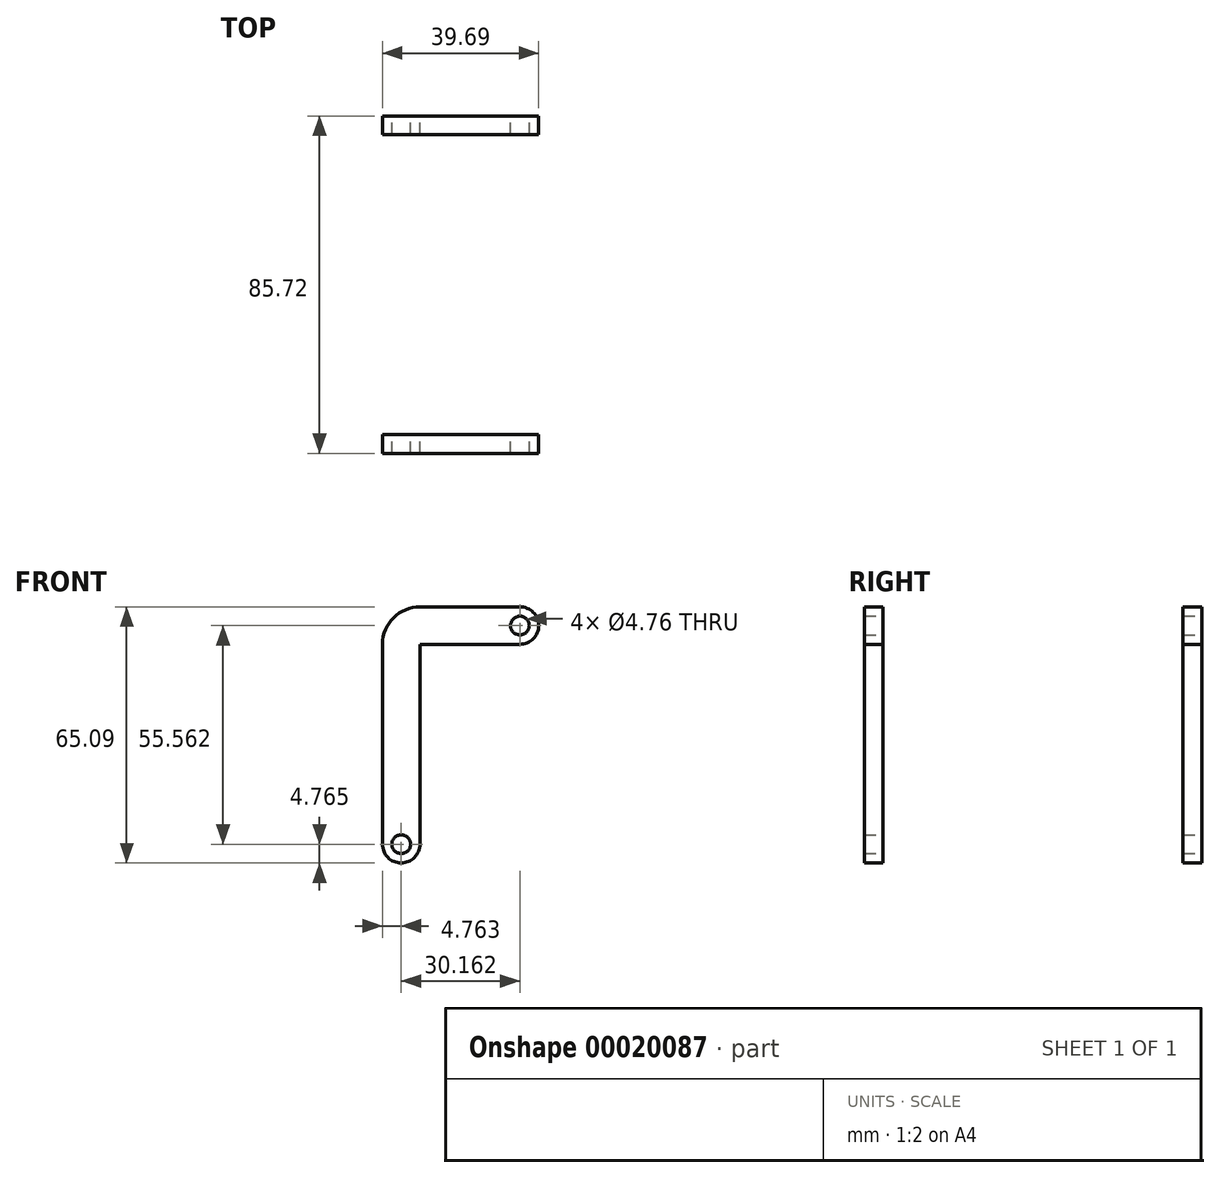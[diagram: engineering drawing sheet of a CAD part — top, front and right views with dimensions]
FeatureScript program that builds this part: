
annotation { "Feature Type Name" : "Feature", "Feature Type Description" : "" }
export const myFeature = defineFeature(function(context is Context, id is Id, definition is map)
    precondition{}
    {
        {
            var Q0;
            Q0=qCreatedBy(makeId("Front.planeOp"),FACE);
            var sketch = newSketch(context, id + "F0", { "sketchPlane" : qUnion([Q0])});
            skLineSegment(sketch, "E0", {"start": v(0, 0) * mm, "end": v(73.6, -19.72) * mm});
            skLineSegment(sketch, "E1", {"start": v(73.6, -19.72) * mm, "end": v(72.37, -24.32) * mm});
            skLineSegment(sketch, "E2", {"start": v(72.37, -24.32) * mm, "end": v(-1.23, -4.6) * mm});
            skLineSegment(sketch, "E3", {"start": v(-1.23, -4.6) * mm, "end": v(0, 0) * mm});
            skSolve(sketch);
        }
        {
            var Q0;
            Q0 = qSketchRegion(id + "F0", true);
            extrude(context, id + "F1", {"entities" : qUnion([Q0]), "endBound" : BoundingType.SYMMETRIC, "depth" : 76.2 * mm});
        }
        {
            var Q0;
            Q0=qCreatedBy(makeId("Front.planeOp"),FACE);
            var sketch = newSketch(context, id + "F2", { "sketchPlane" : qUnion([Q0])});
            skLineSegment(sketch, "E4", {"start": v(0, 3.17) * mm, "end": v(0, 53.98) * mm});
            skLineSegment(sketch, "E5", {"start": v(9.52, 53.98) * mm, "end": v(9.53, 3.18) * mm});
            skArc(sketch, "E6", {"start": v(0, 3.17) * mm, "mid": v(4.76, -1.59) * mm, "end": v(9.53, 3.18) * mm});
            skArc(sketch, "E7", {"start": v(9.52, 63.5) * mm, "mid": v(2.79, 60.71) * mm, "end": v(0, 53.98) * mm});
            skLineSegment(sketch, "E8", {"start": v(9.52, 63.5) * mm, "end": v(34.92, 63.5) * mm});
            skArc(sketch, "E9", {"start": v(34.92, 53.98) * mm, "mid": v(39.69, 58.74) * mm, "end": v(34.92, 63.5) * mm});
            skLineSegment(sketch, "E10", {"start": v(34.92, 53.98) * mm, "end": v(9.52, 53.98) * mm});
            skCircle(sketch, "E11", {"center": v(34.92, 58.74) * mm, "radius": 2.38 * mm});
            skCircle(sketch, "E12", {"center": v(4.76, 3.18) * mm, "radius": 2.38 * mm});
            skSolve(sketch);
        }
        {
            var Q0;
            Q0 = qSketchRegion(id + "F2", true);
            extrude(context, id + "F3", {"entities" : qUnion([Q0]), "endBound" : BoundingType.SYMMETRIC, "depth" : 85.72 * mm});
        }
        {
            var Q0;
            Q0=qCreatedBy(makeId("Front.planeOp"),FACE);
            var sketch = newSketch(context, id + "F4", { "sketchPlane" : qUnion([Q0])});
            skLineSegment(sketch, "E13.bottom", {"start": v(-71.66, -45.41) * mm, "end": v(104, -45.41) * mm});
            skLineSegment(sketch, "E13.top", {"start": v(-71.66, 94.9) * mm, "end": v(104, 94.9) * mm});
            skLineSegment(sketch, "E13.left", {"start": v(-71.66, -45.41) * mm, "end": v(-71.66, 94.9) * mm});
            skLineSegment(sketch, "E13.right", {"start": v(104, -45.41) * mm, "end": v(104, 94.9) * mm});
            skSolve(sketch);
        }
        {
            var Q0;
            Q0 = qSketchRegion(id + "F4", true);
            extrude(context, id + "F5", {"entities" : qUnion([Q0]), "operationType" : NewBodyOperationType.REMOVE, "endBound" : BoundingType.SYMMETRIC, "oppositeDirection" : true, "depth" : 76.2 * mm});
        }
    });
